# Revit family: Bath-Drop_In-Kohler-Mariposa-K_1242-W1
name_source: partatom
category: Plumbing Fixtures
revit_build: Autodesk Revit 2015 (Build: 20140606_1530(x64)
units: mm (PartAtom-declared; Revit-internal decimal feet)

## types (5) — shared parameters
ADA Compliant = Yes
Apparent Load = 120 VA
Assembly Code = D2010510
CW Connection = No
Default Elevation = 0' - 0"
Drain Diameter = 0' - 1 1/2"
Electrical Connector = 120 V, 15A
Electrical Note = Provide one grounded electrical outlet within 24'' (610 mm) of each component
HW Connection = No
Height = 1' - 8"
Keynote = 22 40 00.D2
Length = 5' - 0"
Manufacturer = Kohler
Material = Acrylic
Number of Poles = 1
Product Documentation Link = http://www.us.kohler.com
Product Name = Mariposa 60'' x 36'' Drop-In Bath, Heated Surface
Product Page URL = http://www.us.kohler.com
Sanitary Connector = Sanitary Drain
URL = http://www.us.kohler.com
Vent Connection = Yes
Version = 2014 - v1.0a
Voltage = 120 V
Waste Connection = Yes
Water Capacity = 63 gal (238.5 L)
Weight = 62 lbs (28.1 kg)
Width = 3' - 0"
zero-valued in all types: CWFU, HWFU, Power Factor, WFU

## per-type parameters (varying)
| type | ControlM | Description | Finish | Model |
| 0-White | 0 | 60'' x 36'' Drop-in Bath with Bask Heated Surface and Reversible Drain, White | Acrylic - Kohler - 0 - White | K-1242-W1-0 |
| 47-Almond | 47 | 60'' x 36'' Drop-in Bath with Bask Heated Surface and Reversible Drain, Almond | Acrylic - Kohler - 47 - Almond | K-1242-W1-47 |
| 96-Biscuit | 96 | 60'' x 36'' Drop-in Bath with Bask Heated Surface and Reversible Drain, Biscuit | Acrylic - Kohler - 96 - Biscuit | K-1242-W1-96 |
| G9-Sandbar | 79 | 60'' x 36'' Drop-in Bath with Bask Heated Surface and Reversible Drain, Sandbar | Acrylic - Kohler - G9 - Sandbar | K-1242-W1-G9 |
| NY-Dune | 1425 | 60'' x 36'' Drop-in Bath with Bask Heated Surface and Reversible Drain, Dune | Acrylic - Kohler - NY - Dune | K-1242-W1-NY |

## geometry (parser evidence)
native form markers: Extrusion x5, Sweep x2
no freeform markers — native parametric forms only
